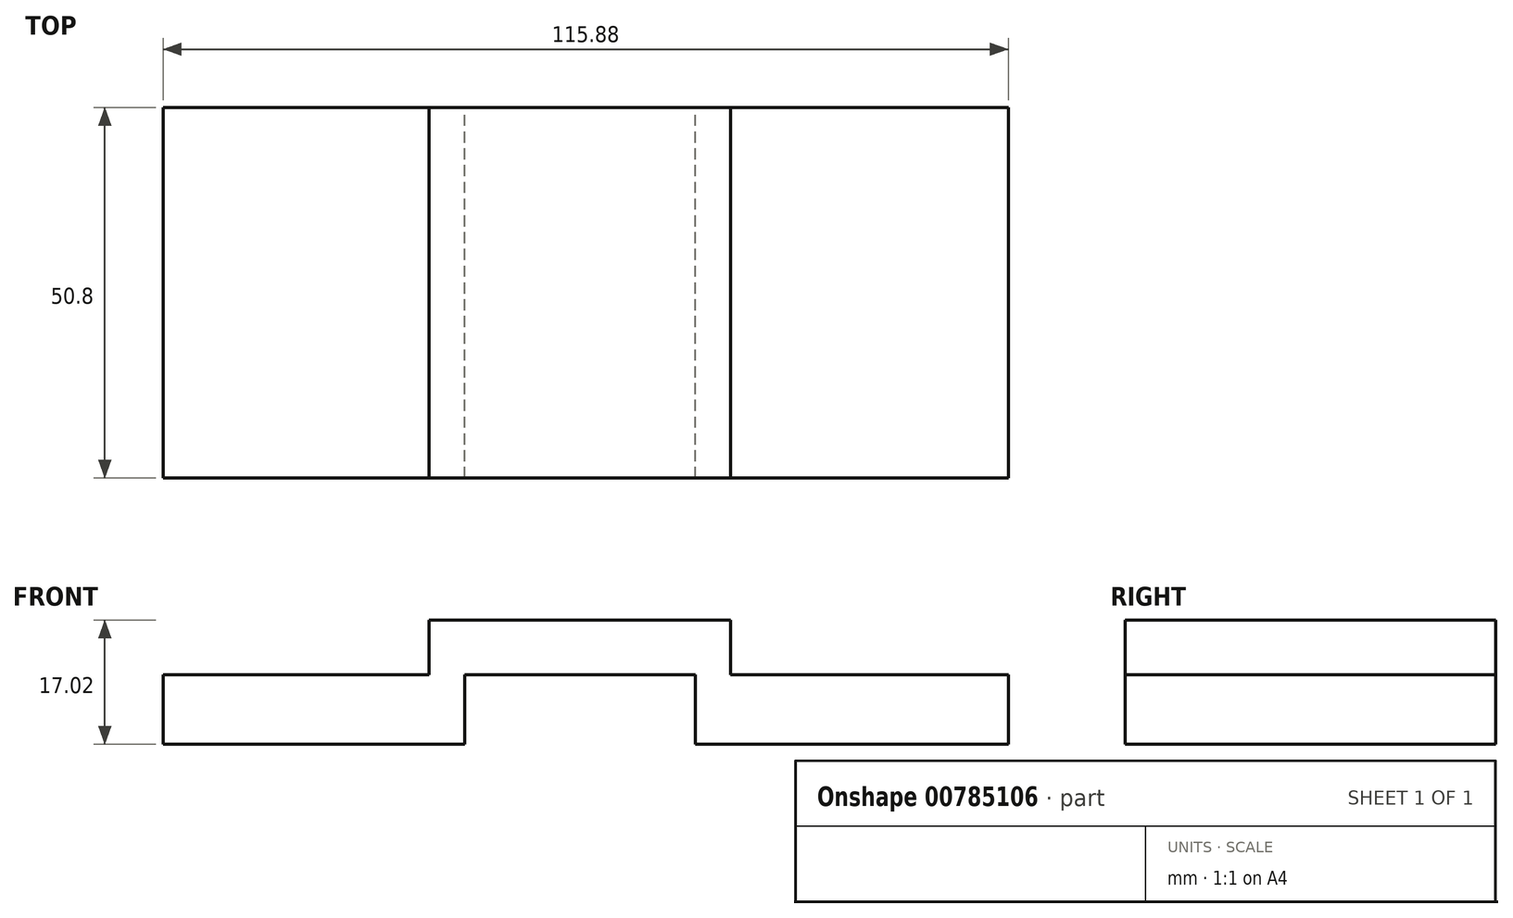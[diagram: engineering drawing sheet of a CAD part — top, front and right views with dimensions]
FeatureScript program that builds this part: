
annotation { "Feature Type Name" : "Feature", "Feature Type Description" : "" }
export const myFeature = defineFeature(function(context is Context, id is Id, definition is map)
    precondition{}
    {
        {
            var Q0;
            Q0=qCreatedBy(makeId("Front.planeOp"),FACE);
            var sketch = newSketch(context, id + "F0", { "sketchPlane" : qUnion([Q0])});
            skLineSegment(sketch, "E0", {"start": v(33.76, 0.38) * mm, "end": v(33.76, 9.92) * mm});
            skLineSegment(sketch, "E1", {"start": v(33.76, 9.92) * mm, "end": v(65.37, 9.92) * mm});
            skLineSegment(sketch, "E2", {"start": v(65.37, 9.92) * mm, "end": v(65.37, 0.38) * mm});
            skLineSegment(sketch, "E3", {"start": v(28.82, 9.92) * mm, "end": v(28.82, 17.4) * mm});
            skLineSegment(sketch, "E4", {"start": v(28.82, 17.4) * mm, "end": v(70.16, 17.4) * mm});
            skLineSegment(sketch, "E5", {"start": v(70.16, 17.4) * mm, "end": v(70.16, 9.92) * mm});
            skLineSegment(sketch, "E6", {"start": v(28.82, 9.92) * mm, "end": v(-7.62, 9.92) * mm});
            skLineSegment(sketch, "E7", {"start": v(-7.62, 9.92) * mm, "end": v(-7.62, 0.38) * mm});
            skLineSegment(sketch, "E8", {"start": v(-7.62, 0.38) * mm, "end": v(33.76, 0.38) * mm});
            skLineSegment(sketch, "E9", {"start": v(70.16, 9.92) * mm, "end": v(108.26, 9.92) * mm});
            skLineSegment(sketch, "E10", {"start": v(108.26, 9.92) * mm, "end": v(108.26, 0.38) * mm});
            skLineSegment(sketch, "E11", {"start": v(108.26, 0.38) * mm, "end": v(65.37, 0.38) * mm});
            skPoint(sketch, "E12", {"position": v(2.06, 7.56) * mm});
            skSolve(sketch);
        }
        {
            var Q0;
            Q0 = qSketchRegion(id + "F0", true);
            extrude(context, id + "F1", {"entities" : qUnion([Q0]), "depth" : 50.8 * mm, "offsetDistance" : 25.4 * mm});
        }
    });
